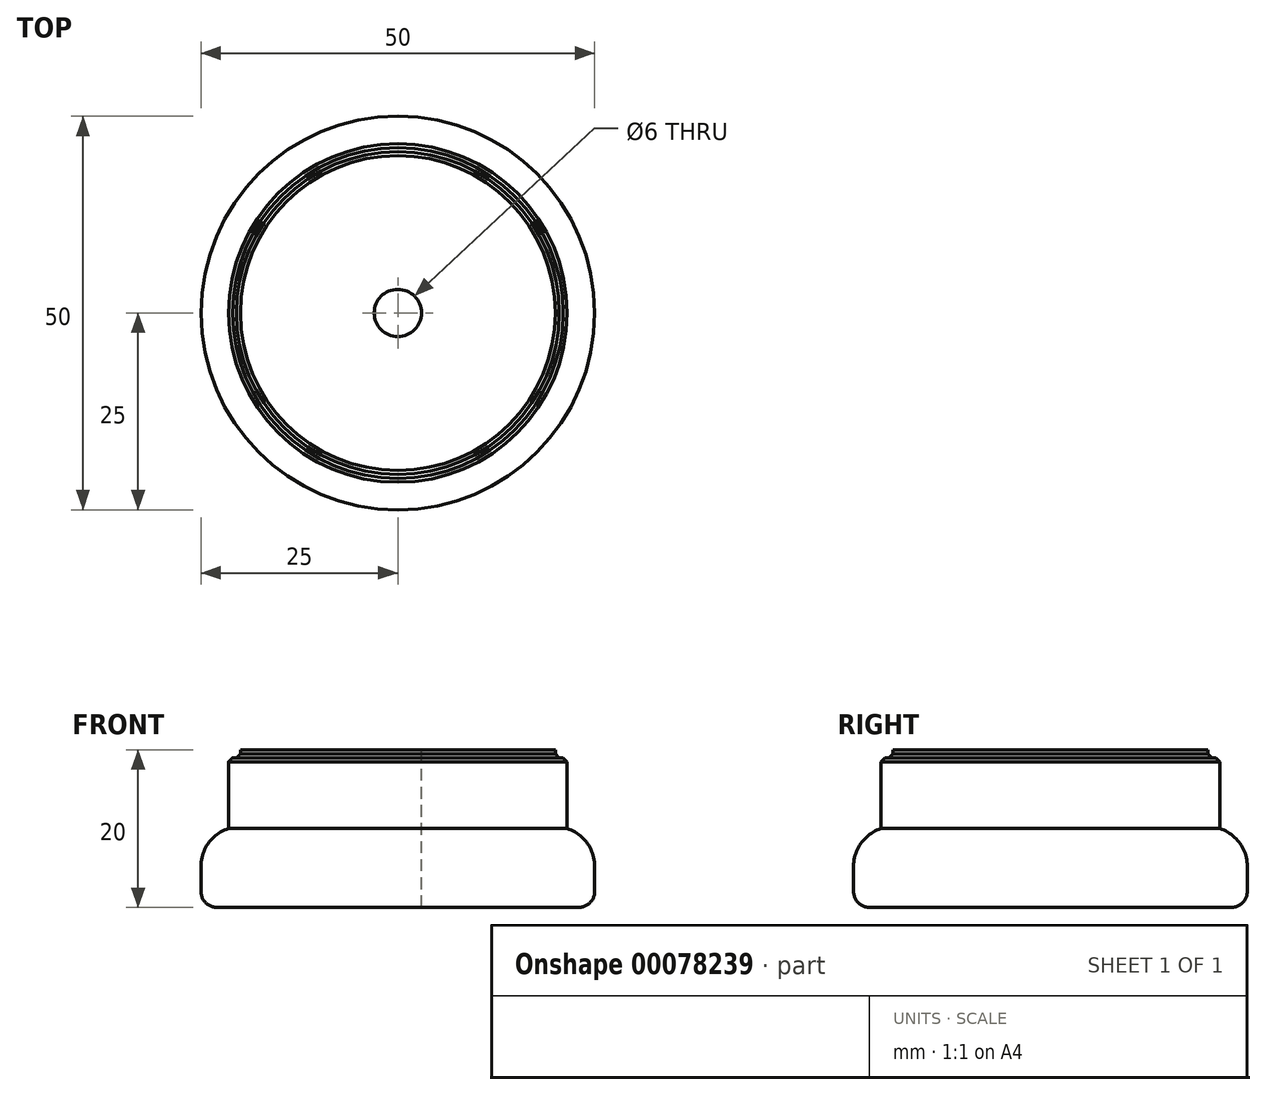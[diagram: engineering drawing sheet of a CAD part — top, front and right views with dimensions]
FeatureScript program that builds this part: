
annotation { "Feature Type Name" : "Feature", "Feature Type Description" : "" }
export const myFeature = defineFeature(function(context is Context, id is Id, definition is map)
    precondition{}
    {
        {
            var Q0;
            Q0=qCreatedBy(makeId("Front.planeOp"),FACE);
            var sketch = newSketch(context, id + "F0", { "sketchPlane" : qUnion([Q0])});
            skLineSegment(sketch, "E0.bottom", {"start": v(0, 0) * mm, "end": v(25, 0) * mm});
            skLineSegment(sketch, "E0.right", {"start": v(25, 0) * mm, "end": v(25, 10) * mm});
            skLineSegment(sketch, "E1", {"start": v(25, 10) * mm, "end": v(21.5, 10) * mm});
            skLineSegment(sketch, "E2", {"start": v(21.5, 10) * mm, "end": v(21.5, 19) * mm});
            skLineSegment(sketch, "E3", {"start": v(21.5, 19) * mm, "end": v(20, 19) * mm});
            skLineSegment(sketch, "E4", {"start": v(20, 19) * mm, "end": v(20, 20) * mm});
            skLineSegment(sketch, "E5", {"start": v(20, 20) * mm, "end": v(0, 20) * mm});
            skLineSegment(sketch, "E6", {"start": v(0, 34.87) * mm, "end": v(0, -12.62) * mm, "construction": true});
            skLineSegment(sketch, "E7", {"start": v(0, 20) * mm, "end": v(0, 0) * mm});
            skSolve(sketch);
        }
        {
            var Q0;
            Q0 = qSketchRegion(id + "F0", true);
            var Q1;
            Q1=sQuery(id+"F0.wireOp",EDGE,"E6");
            revolve(context, id + "F1", {"entities" : qUnion([Q0]), "axis" : qUnion([Q1]), "revolveType" : RevolveType.FULL});
        }
        {
            var Q0;
            Q0=makeQuery(id+"F1.opRevolve","SWEPT_EDGE",EDGE,{"disambiguationData":[OSD([sQuery(id+"F0.wireOp",EDGE,"E0.right"),sQuery(id+"F0.wireOp",EDGE,"E1")])]});
            fillet(context, id + "F2", {"entities" : qUnion([Q0]), "radius" : 5 * mm, "tangentPropagation" : true, "allowEdgeOverflow" : false});
        }
        {
            var Q0;
            Q0=makeQuery(id+"F1.opRevolve","SWEPT_EDGE",EDGE,{"disambiguationData":[OSD([sQuery(id+"F0.wireOp",EDGE,"E0.bottom"),sQuery(id+"F0.wireOp",EDGE,"E0.right")])]});
            fillet(context, id + "F3", {"entities" : qUnion([Q0]), "radius" : 2 * mm, "tangentPropagation" : true, "allowEdgeOverflow" : false});
        }
        {
            var Q0;
            Q0=makeQuery(id+"F1.opRevolve","SWEPT_EDGE",EDGE,{"disambiguationData":[OSD([sQuery(id+"F0.wireOp",EDGE,"E2"),sQuery(id+"F0.wireOp",EDGE,"E3")])]});
            var Q1;
            Q1=makeQuery(id+"F1.opRevolve","SWEPT_EDGE",EDGE,{"disambiguationData":[OSD([sQuery(id+"F0.wireOp",EDGE,"E3"),sQuery(id+"F0.wireOp",EDGE,"E4")])]});
            chamfer(context, id + "F4", {"entities" : qUnion([Q0, Q1]), "width" : .5 * mm, "tangentPropagation" : true});
        }
        {
            var Q0;
            Q0=makeQuery(id+"F1.opRevolve","SWEPT_FACE",FACE,{"disambiguationData":[OSD([sQuery(id+"F0.wireOp",EDGE,"E5")])]});
            var sketch = newSketch(context, id + "F5", { "sketchPlane" : qUnion([Q0])});
            skCircle(sketch, "E8", {"center": v(0, 0) * mm, "radius": 3 * mm});
            skSolve(sketch);
        }
        {
            var Q0;
            Q0 = qSketchRegion(id + "F5", true);
            extrude(context, id + "F6", {"entities" : qUnion([Q0]), "operationType" : NewBodyOperationType.REMOVE, "endBound" : BoundingType.THROUGH_ALL, "oppositeDirection" : true, "depth" : 25 * mm});
        }
    });
